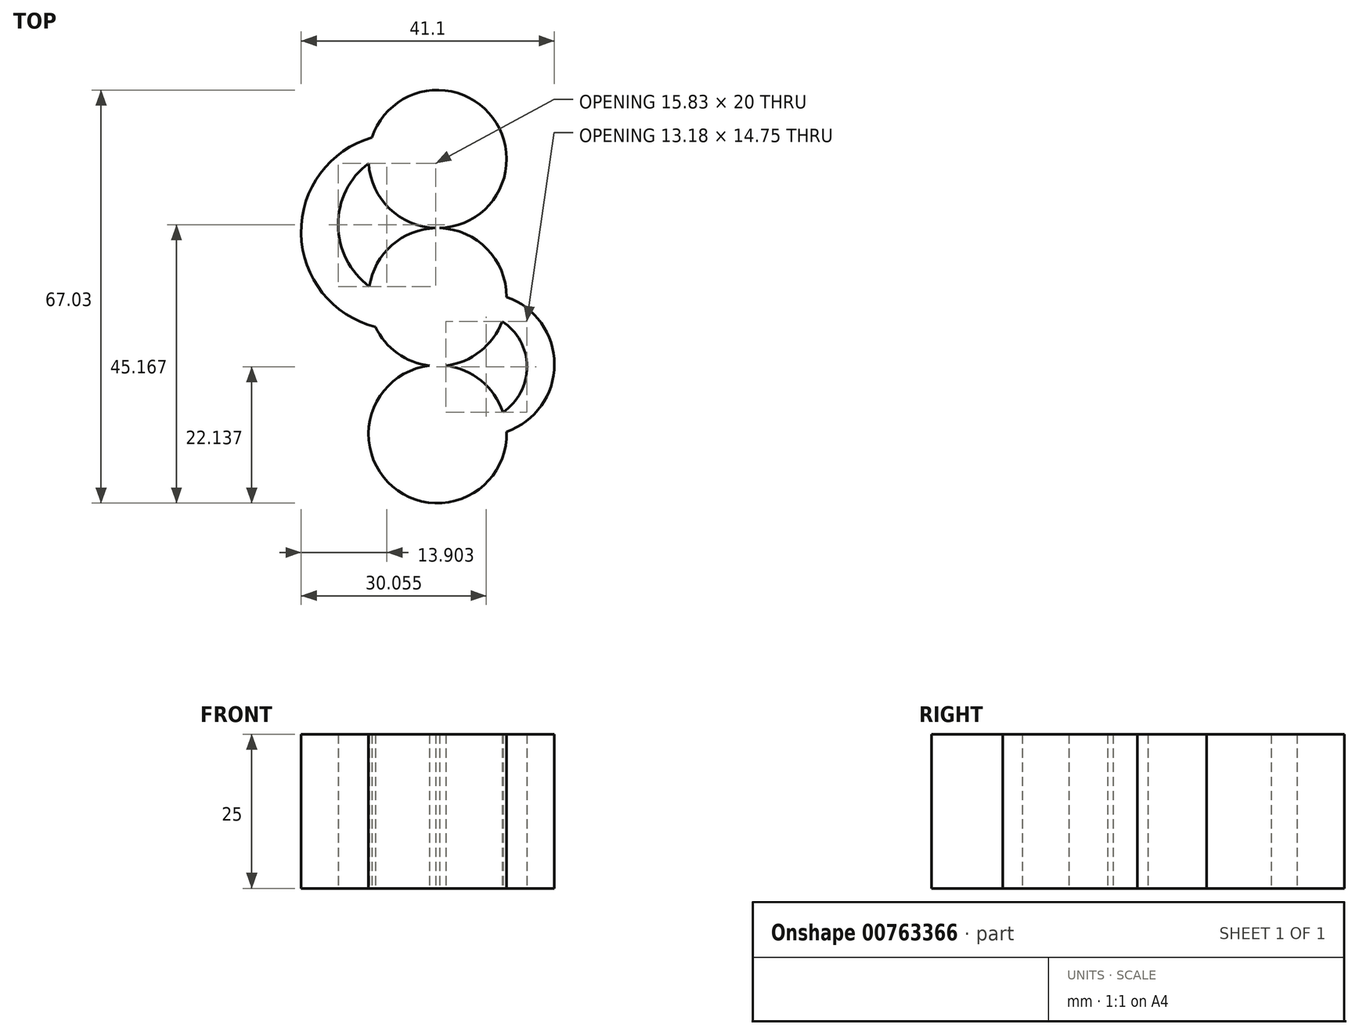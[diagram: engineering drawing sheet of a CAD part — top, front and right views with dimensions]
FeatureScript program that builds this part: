
annotation { "Feature Type Name" : "Feature", "Feature Type Description" : "" }
export const myFeature = defineFeature(function(context is Context, id is Id, definition is map)
    precondition{}
    {
        {
            var Q0;
            Q0=qCreatedBy(makeId("Top.planeOp"),FACE);
            var sketch = newSketch(context, id + "F0", { "sketchPlane" : qUnion([Q0])});
            skCircle(sketch, "E0", {"center": v(0, 0) * mm, "radius": 11.2 * mm});
            skCircle(sketch, "E1", {"center": v(0, 22.4) * mm, "radius": 11.2 * mm});
            skCircle(sketch, "E2", {"center": v(0, -22.24) * mm, "radius": 11.2 * mm});
            skArc(sketch, "E3", {"start": v(-11.18, 21.73) * mm, "mid": v(-16.14, 11.7) * mm, "end": v(-11.07, 1.72) * mm});
            skArc(sketch, "E4", {"start": v(-10.64, 25.9) * mm, "mid": v(-22.13, 10.33) * mm, "end": v(-10.1, -4.84) * mm});
            skArc(sketch, "E5", {"start": v(10.62, -18.68) * mm, "mid": v(14.52, -11.27) * mm, "end": v(10.49, -3.93) * mm});
            skArc(sketch, "E6", {"start": v(11.2, -21.85) * mm, "mid": v(18.97, -10.93) * mm, "end": v(11.2, 0) * mm});
            skSolve(sketch);
        }
        {
            var Q0;
            Q0 = qSketchRegion(id + "F0", true);
            extrude(context, id + "F1", {"entities" : qUnion([Q0]), "depth" : 25 * mm, "offsetDistance" : 25 * mm});
        }
    });
